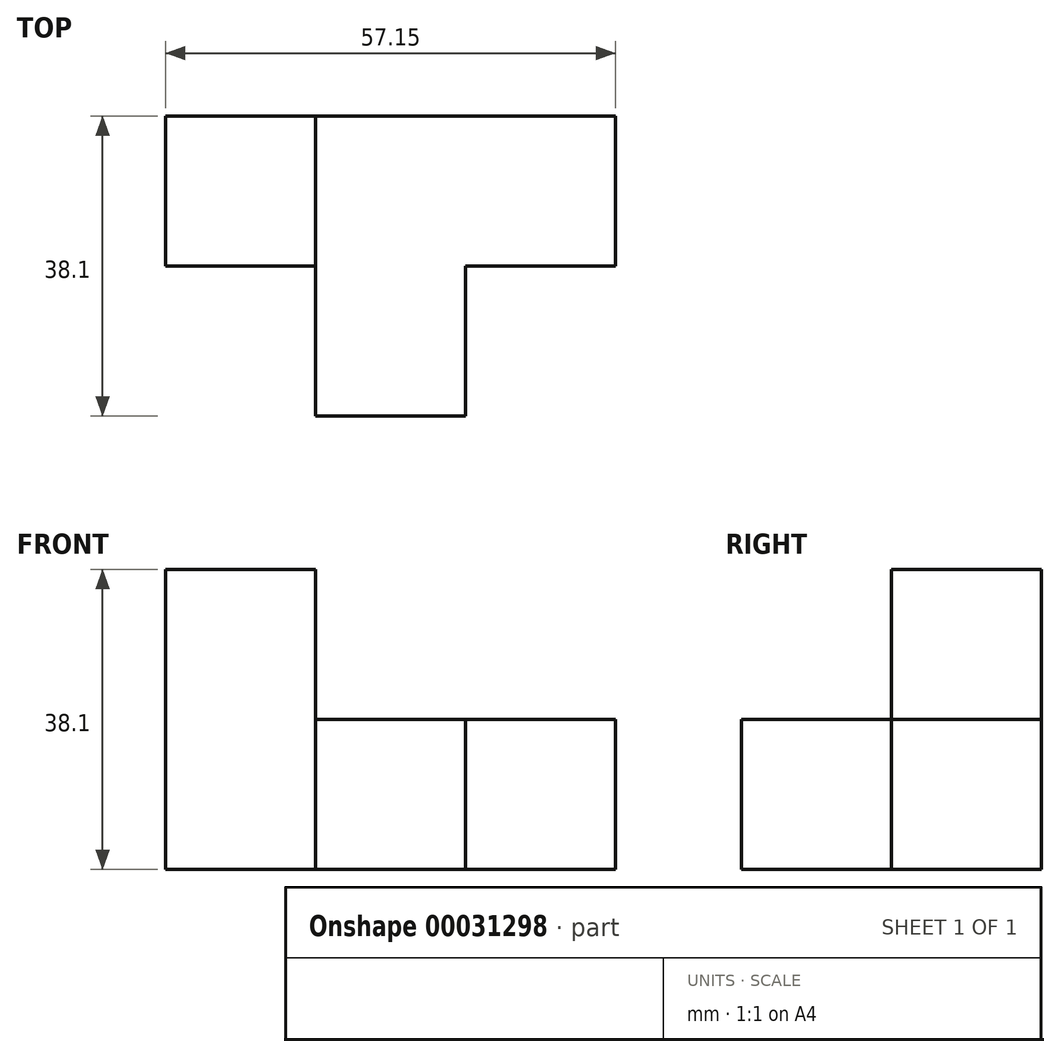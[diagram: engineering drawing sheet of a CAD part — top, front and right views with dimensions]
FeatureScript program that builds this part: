
annotation { "Feature Type Name" : "Feature", "Feature Type Description" : "" }
export const myFeature = defineFeature(function(context is Context, id is Id, definition is map)
    precondition{}
    {
        {
            var Q0;
            Q0=qCreatedBy(makeId("Top.planeOp"),FACE);
            var sketch = newSketch(context, id + "F0", { "sketchPlane" : qUnion([Q0])});
            skLineSegment(sketch, "E0", {"start": v(0, 0) * mm, "end": v(0, 19.05) * mm});
            skLineSegment(sketch, "E1", {"start": v(0, 19.05) * mm, "end": v(57.15, 19.05) * mm});
            skLineSegment(sketch, "E2", {"start": v(57.15, 19.05) * mm, "end": v(57.15, 0) * mm});
            skLineSegment(sketch, "E3", {"start": v(57.15, 0) * mm, "end": v(38.1, 0) * mm});
            skLineSegment(sketch, "E4", {"start": v(38.1, 0) * mm, "end": v(38.1, -19.05) * mm});
            skLineSegment(sketch, "E5", {"start": v(38.1, -19.05) * mm, "end": v(19.05, -19.05) * mm});
            skLineSegment(sketch, "E6", {"start": v(19.05, -19.05) * mm, "end": v(19.05, 0) * mm});
            skLineSegment(sketch, "E7", {"start": v(19.05, 0) * mm, "end": v(0, 0) * mm});
            skSolve(sketch);
        }
        {
            var Q0;
            Q0=makeQuery(id+"F0.imprint","IMPRINT",FACE,{"disambiguationData":[TD([[makeQuery(id+"F0.imprint","IMPRINT",EDGE,{"derivedFrom":sQuery(id+"F0.wireOp",EDGE,"E0")}),-1.0]])]});
            extrude(context, id + "F1", {"entities" : qUnion([Q0]), "depth" : 19.05 * mm});
        }
        {
            var Q0;
            Q0=makeQuery(id+"F1.opExtrude","CAP_FACE",FACE,{"disambiguationData":[OSD([sQuery(id+"F0.wireOp",EDGE,"E0"),sQuery(id+"F0.wireOp",EDGE,"E1"),sQuery(id+"F0.wireOp",EDGE,"E2"),sQuery(id+"F0.wireOp",EDGE,"E3"),sQuery(id+"F0.wireOp",EDGE,"E4"),sQuery(id+"F0.wireOp",EDGE,"E5"),sQuery(id+"F0.wireOp",EDGE,"E6"),sQuery(id+"F0.wireOp",EDGE,"E7")])],"isStart":false});
            var sketch = newSketch(context, id + "F2", { "sketchPlane" : qUnion([Q0])});
            skLineSegment(sketch, "E8", {"start": v(0, 19.05) * mm, "end": v(0, 0) * mm});
            skLineSegment(sketch, "E9", {"start": v(0, 0) * mm, "end": v(19.05, 0) * mm});
            skLineSegment(sketch, "E10", {"start": v(19.05, 0) * mm, "end": v(19.05, 19.05) * mm});
            skLineSegment(sketch, "E11", {"start": v(19.05, 19.05) * mm, "end": v(0, 19.05) * mm});
            skSolve(sketch);
        }
        {
            var Q0;
            Q0=makeQuery(id+"F2.imprint","IMPRINT",FACE,{"disambiguationData":[TD([[makeQuery(id+"F2.imprint","IMPRINT",EDGE,{"derivedFrom":sQuery(id+"F2.wireOp",EDGE,"E8")}),-1.0]])]});
            extrude(context, id + "F3", {"entities" : qUnion([Q0]), "operationType" : NewBodyOperationType.ADD, "depth" : 19.05 * mm});
        }
    });
